# Revit family: Compact vitreous china bidet - Hall - Roca - 357624xx0
name_source: partatom
category: Plumbing Fixtures
revit_build: Autodesk Revit Architecture 2014 (Build: 20130308_1515(x64)
units: mm (PartAtom-declared; Revit-internal decimal feet)

## types (4) — shared parameters
BIMobject category = Bidets
Date of publishing = 2012-06-01
Description = Compact vitreous china bidet
Eco green certification = No
Height = 400 mm  [stored 1.31234 ft]
IFC Classification = Furnishing Element
Installation instructions = http://www.roca.com
Installation type = Floorstanding
Length = 355 mm  [stored 1.1647 ft]
Manufacturer name = Roca
Manufacturer url = http://www.roca.com
Model = 357624...
NBS Reference Code = 35-65-70-10
NBS Reference Description = Bidet Systems
Nominal height = 400.00
Nominal width = 525.00
Outlet Diameter = 46 mm  [stored 0.150919 ft]
Product Guid = e95b059d-2ee3-4e50-b246-26a9476caf7e
Product data url = http://bimobject.com
Product family = Hall
Product group = BIDETS
QR code = http://bimobject.com
Shape = Square
Suitable for Children = No
Suitable for Handicapped = No
Taphole configuration = 1 Taphole
Taphole configuration: 1 Taphole
Tapholes Diameter = 35 mm  [stored 0.114829 ft]
Technical description = http://www.roca.com
UNSPSC Code = 301815
UNSPSC Name = Sanitary ware
URL = http://www.roca.com
Uniclass 1.4 Code = L7215
Uniclass 1.4 Description = Bidets
Uniclass 2.0 Code = SS-35-65-70-10
Uniclass 2.0 Description = Bidet Systems
Weight Net (Kg) = 0
Width = 525 mm
zero-valued in all types: Edition number

## per-type parameters (varying)
| type | Product SKU |
| White - Hall - Roca | A357624000 |
| Pergamon - Hall - Roca | A357624170 |
| Graphit - Hall - Roca | A357624920 |
| Edelweiss - Hall - Roca | A357624910 |

note: column(s) folded — value = type name in every type: Material

note: [stored X ft] marks values corroborated as IEEE doubles in the binary element streams (Revit-internal decimal feet)

## geometry (parser evidence)
native form markers: Sweep x2
no freeform markers — native parametric forms only
